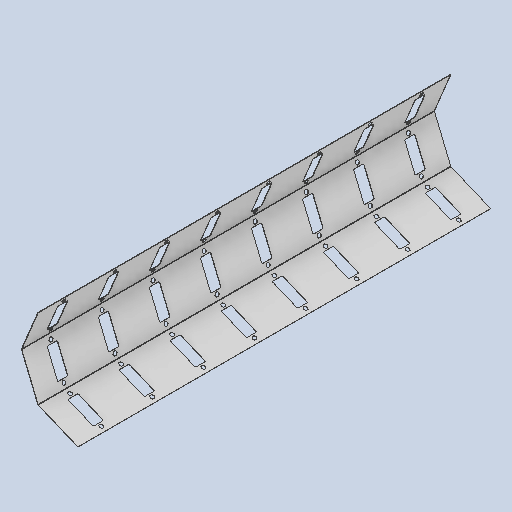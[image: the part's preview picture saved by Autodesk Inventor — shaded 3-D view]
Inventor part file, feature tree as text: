
AUTODESK INVENTOR PART (.ipt)
format: ipt  version: 2025 (Build 290162010, 162A)  size: 973,312 bytes
history: native  units: mm
features: sheet_metal_op x3, sketch x3, other x2, extrude x1, fillet x1, pattern_circular x1, pattern_linear x1, chamfer x1, projected_geometry x1
ambient origin geometry x8: Origin, YZ Plane, XZ Plane, XY Plane, X Axis, Y Axis, Z Axis, Center Point
bodies: Body1 (feature_tree)
feature tree (14):
  sheet_metal_op  "Contour Flange3"
  extrude  "Extrusion4"  Depth=4.0mm
  fillet  "Fillet1"  Radius=0.9mm
  pattern_circular  "Circular Pattern2"  [2 undecoded]
  pattern_linear  "Rectangular Pattern2"  Spacing1=2.0mm  [1 undecoded]
  chamfer  "Corner Round1"
  sketch  "Sketch2"  dims[d58=4.0mm d59=4.0mm d70=0.9mm]
  other  "Plate6"
  sheet_metal_op  "Bend6"
  sheet_metal_op  "Corner6"
  sketch  "Sketch11"  dims[d72=0.9mm]
  projected_geometry  "Projected Loop1"
  other  "Definition1"
  sketch  "Sketch11:Copy"  dims[d74=513.0mm d75=2.0mm d76=2.0mm d77=1.0mm d78=4.0mm d79=2.0mm d80=2020.0mm d81=2.0mm d82=3.0mm d83=8.0mm d84=2.0mm d85=2.0mm d141=50.0mm d142=135.0mm d145=125.0mm d147=10.0mm d148=0.0mm d149=5.0mm d150=30.0mm d151=90.0deg d153=80.0mm d155=250.0mm d156=2.0mm d157=206.278354mm d159=16.8mm d160=16.8mm d161=165.0mm]
note: 3 required parameter values undecoded (feature->parameter linkage not recoverable at this tier; creation-order binding heuristic only, values carry confidence <= 0.55)
